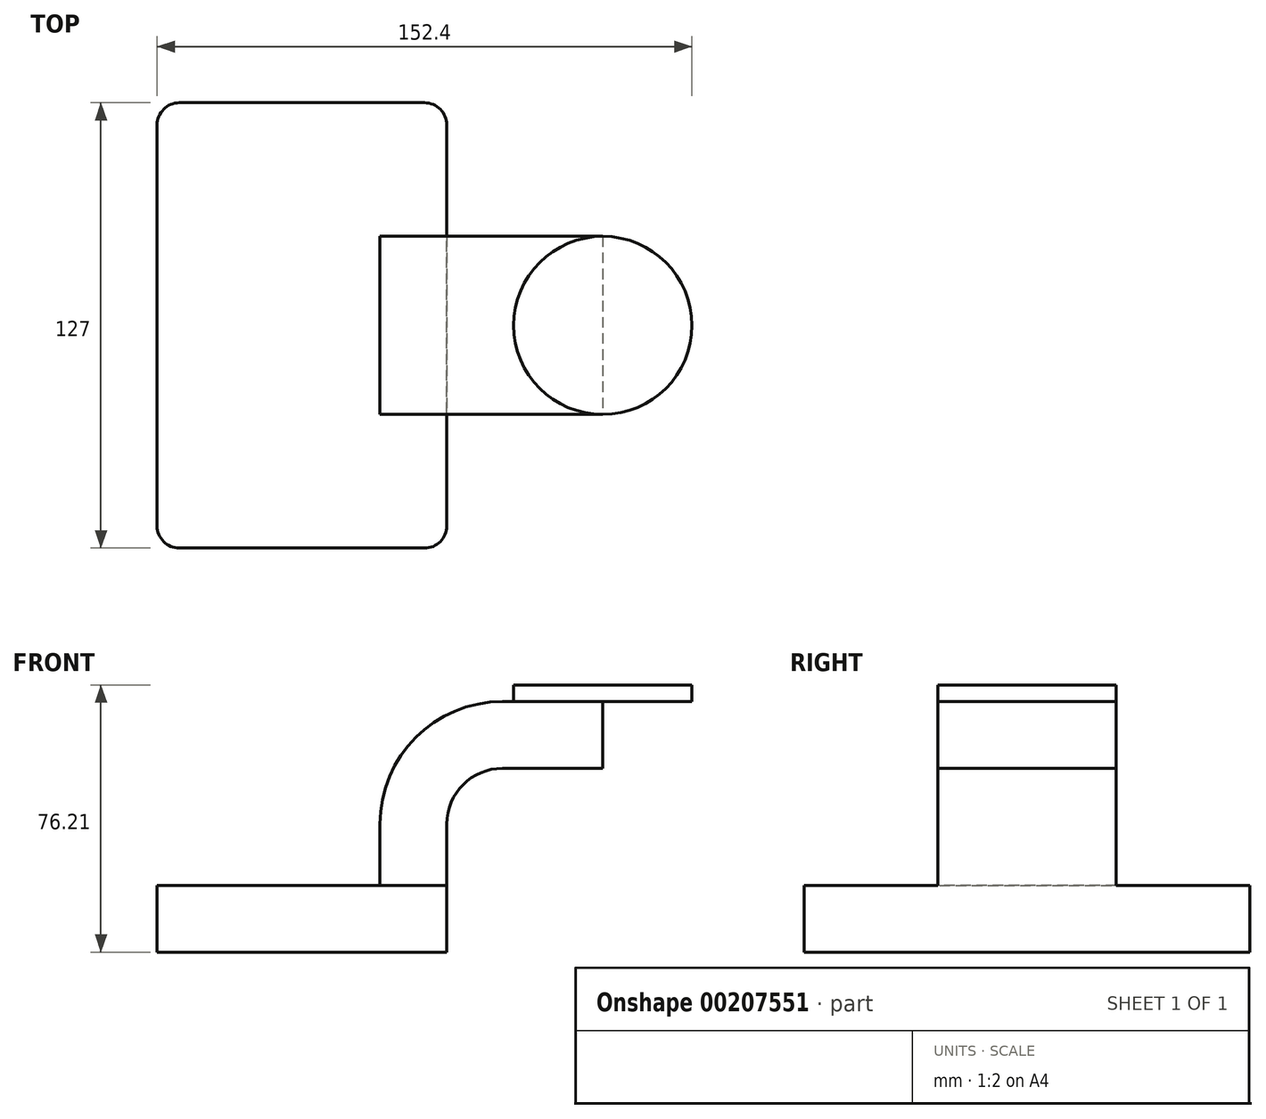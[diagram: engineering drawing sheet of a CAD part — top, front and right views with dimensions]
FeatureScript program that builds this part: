
annotation { "Feature Type Name" : "Feature", "Feature Type Description" : "" }
export const myFeature = defineFeature(function(context is Context, id is Id, definition is map)
    precondition{}
    {
        {
            var Q0;
            Q0=qCreatedBy(makeId("Front.planeOp"),FACE);
            var sketch = newSketch(context, id + "F0", { "sketchPlane" : qUnion([Q0])});
            skLineSegment(sketch, "E0.bottom", {"start": v(41.28, -9.52) * mm, "end": v(-41.28, -9.53) * mm});
            skLineSegment(sketch, "E0.top", {"start": v(41.28, 9.53) * mm, "end": v(-41.28, 9.53) * mm});
            skLineSegment(sketch, "E0.left", {"start": v(41.28, -9.52) * mm, "end": v(41.28, 9.53) * mm});
            skLineSegment(sketch, "E0.right", {"start": v(-41.28, -9.52) * mm, "end": v(-41.28, 9.53) * mm});
            skPoint(sketch, "E0.middle", {"position": v(0, 0) * mm});
            skLineSegment(sketch, "E1.bottom", {"start": v(111.12, 66.68) * mm, "end": v(60.33, 66.68) * mm});
            skLineSegment(sketch, "E1.top", {"start": v(111.12, 38.1) * mm, "end": v(60.33, 38.1) * mm});
            skLineSegment(sketch, "E1.left", {"start": v(111.12, 66.67) * mm, "end": v(111.12, 38.1) * mm});
            skLineSegment(sketch, "E1.right", {"start": v(60.32, 66.68) * mm, "end": v(60.33, 38.1) * mm});
            skPoint(sketch, "E1.middle", {"position": v(85.72, 52.39) * mm});
            skLineSegment(sketch, "E2", {"start": v(41.28, 9.53) * mm, "end": v(41.28, 27) * mm});
            skArc(sketch, "E3", {"start": v(41.27, 27) * mm, "mid": v(45.92, 38.23) * mm, "end": v(57.15, 42.88) * mm});
            skLineSegment(sketch, "E4", {"start": v(57.15, 42.88) * mm, "end": v(85.72, 42.88) * mm});
            skLineSegment(sketch, "E5.0", {"start": v(60.32, 66.68) * mm, "end": v(88.9, 66.68) * mm});
            skLineSegment(sketch, "E5.2", {"start": v(17.48, 9.53) * mm, "end": v(17.48, 27) * mm});
            skLineSegment(sketch, "E6.0", {"start": v(57.15, 61.93) * mm, "end": v(85.72, 61.93) * mm});
            skArc(sketch, "E6.1", {"start": v(22.23, 27) * mm, "mid": v(32.45, 51.7) * mm, "end": v(57.15, 61.93) * mm});
            skLineSegment(sketch, "E6.2", {"start": v(22.22, 9.53) * mm, "end": v(22.22, 27) * mm});
            skLineSegment(sketch, "E7", {"start": v(85.72, 38.1) * mm, "end": v(85.72, 66.68) * mm});
            skLineSegment(sketch, "E8", {"start": v(10.76, 51.1) * mm, "end": v(10.76, 51.1) * mm});
            skFitSpline(sketch, "E9", {"points": [v(-41.28, 9.53) * mm, v(60.32, 66.67) * mm], "startDerivative": vector(10.84, 20.4) * mm, "endDerivative": vector(130.07, -7.9) * mm});
            skSolve(sketch);
        }
        {
            var Q0;
            Q0=makeQuery(id+"F0.imprint","IMPRINT",FACE,{"disambiguationData":[TD([[makeQuery(id+"F0.imprint","IMPRINT",EDGE,{"derivedFrom":sQuery(id+"F0.wireOp",EDGE,"E0.bottom")}),-1.0]])]});
            extrude(context, id + "F1", {"entities" : qUnion([Q0]), "endBound" : BoundingType.SYMMETRIC, "depth" : 127 * mm});
        }
        {
            var Q0;
            {var subQ1=sQuery(id+"F0.wireOp",EDGE,"E2");Q0=makeQuery(id+"F0.imprint","IMPRINT",FACE,{"disambiguationData":[TD([[makeQuery(id+"F0.imprint","IMPRINT",EDGE,{"derivedFrom":subQ1}),1.0]])]});}
            var Q1;
            {var subQ0=sQuery(id+"F0.wireOp",EDGE,"E4");var subQ1=sQuery(id+"F0.wireOp",EDGE,"E1.right");var subQ2=makeQuery(id+"F0.imprint","INTERSECT",VERTEX,{"derivedFrom":[subQ1,subQ0]});Q1=makeQuery(id+"F0.imprint","IMPRINT",FACE,{"disambiguationData":[TD([[makeQuery(id+"F0.imprint","IMPRINT",EDGE,{"disambiguationData":[TD([[subQ2,1.0]])],"derivedFrom":subQ1}),1.0]])]});}
            extrude(context, id + "F2", {"entities" : qUnion([Q0, Q1]), "operationType" : NewBodyOperationType.ADD, "endBound" : BoundingType.SYMMETRIC, "oppositeDirection" : true, "depth" : 50.8 * mm});
        }
        {
            var Q0;
            {var subQ0=sQuery(id+"F0.wireOp",EDGE,"E6.1");Q0=makeQuery(id+"F0.imprint","IMPRINT",FACE,{"disambiguationData":[TD([[makeQuery(id+"F0.imprint","IMPRINT",EDGE,{"derivedFrom":subQ0}),1.0]])]});}
            extrude(context, id + "F3", {"entities" : qUnion([Q0]), "operationType" : NewBodyOperationType.ADD, "endBound" : BoundingType.SYMMETRIC, "depth" : 15.88 * mm});
        }
        {
            var Q0;
            {var subQ1=sQuery(id+"F0.wireOp",EDGE,"E1.bottom");Q0=makeQuery(id+"F0.imprint","IMPRINT",FACE,{"disambiguationData":[TD([[makeQuery(id+"F0.imprint","IMPRINT",EDGE,{"derivedFrom":subQ1}),1.0]])]});}
            var Q1;
            Q1=sQuery(id+"F0.wireOp",EDGE,"E7");
            revolve(context, id + "F4", {"entities" : qUnion([Q0]), "axis" : qUnion([Q1]), "revolveType" : RevolveType.FULL});
        }
        {
            var Q0;
            Q0=makeQuery(id+"F1.opExtrude","CAP_EDGE",EDGE,{"disambiguationData":[OSD([sQuery(id+"F0.wireOp",EDGE,"E0.right")])],"isStart":false});
            var Q1;
            Q1=makeQuery(id+"F1.opExtrude","CAP_EDGE",EDGE,{"disambiguationData":[OSD([sQuery(id+"F0.wireOp",EDGE,"E0.left")])],"isStart":false});
            var Q2;
            Q2=makeQuery(id+"F1.opExtrude","CAP_EDGE",EDGE,{"disambiguationData":[OSD([sQuery(id+"F0.wireOp",EDGE,"E0.right")])],"isStart":true});
            var Q3;
            Q3=makeQuery(id+"F1.opExtrude","CAP_EDGE",EDGE,{"disambiguationData":[OSD([sQuery(id+"F0.wireOp",EDGE,"E0.left")])],"isStart":true});
            fillet(context, id + "F5", {"entities" : qUnion([Q0, Q1, Q2, Q3]), "radius" : 6.35 * mm, "tangentPropagation" : true, "allowEdgeOverflow" : false});
        }
    });
